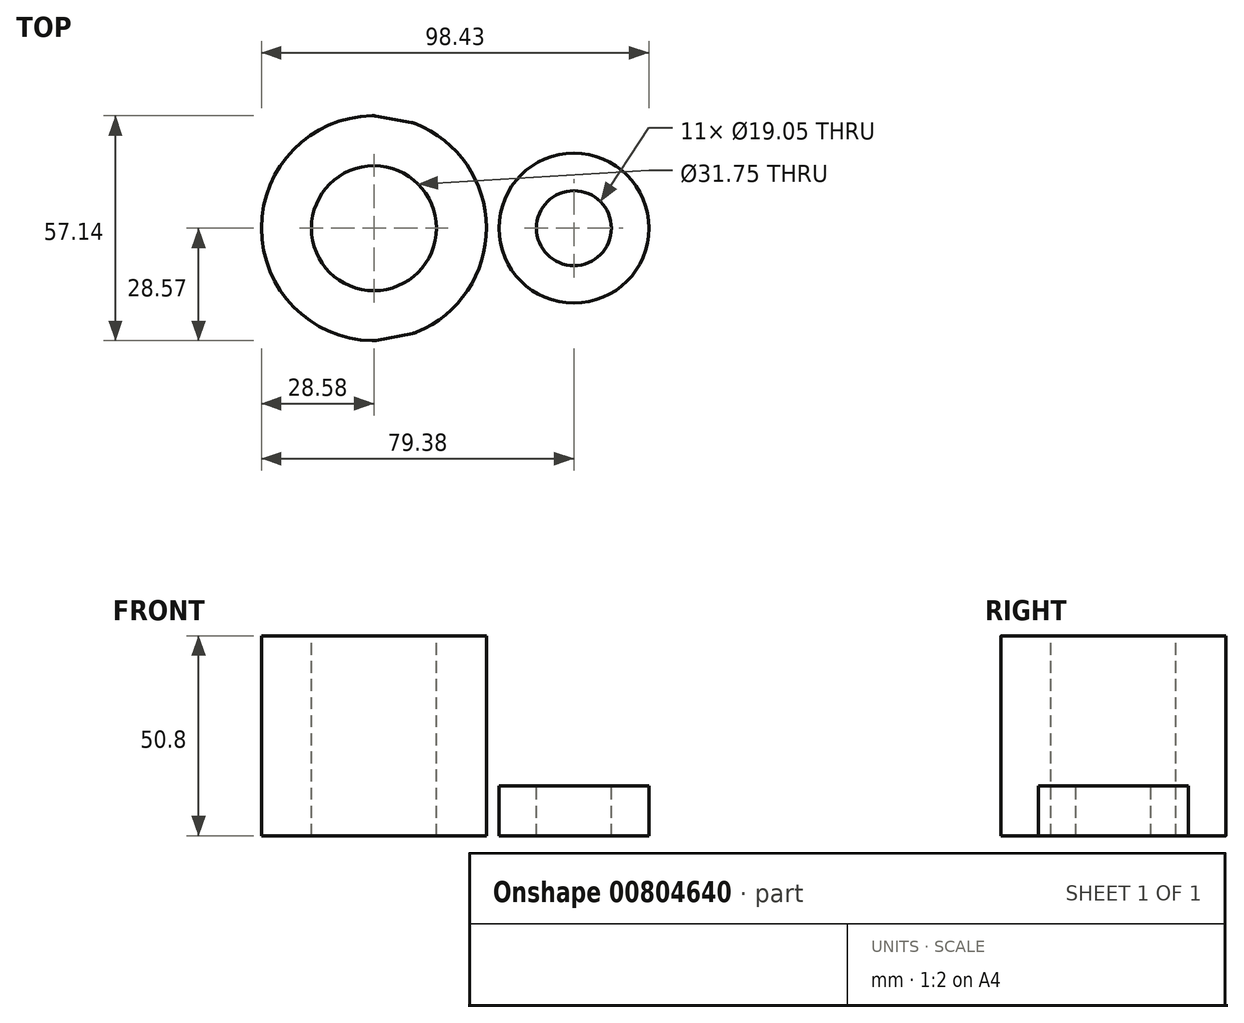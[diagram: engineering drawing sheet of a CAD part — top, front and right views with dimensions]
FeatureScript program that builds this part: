
annotation { "Feature Type Name" : "Feature", "Feature Type Description" : "" }
export const myFeature = defineFeature(function(context is Context, id is Id, definition is map)
    precondition{}
    {
        {
            var Q0;
            Q0=qCreatedBy(makeId("Top.planeOp"),FACE);
            var sketch = newSketch(context, id + "F0", { "sketchPlane" : qUnion([Q0])});
            skCircle(sketch, "E0", {"center": v(0, 0) * mm, "radius": 28.58 * mm});
            skCircle(sketch, "E1", {"center": v(50.8, 0) * mm, "radius": 19.05 * mm});
            skLineSegment(sketch, "E2", {"start": v(0, 28.58) * mm, "end": v(54.2, 18.74) * mm});
            skLineSegment(sketch, "E3", {"start": v(0, -28.57) * mm, "end": v(50.8, -19.05) * mm});
            skCircle(sketch, "E4", {"center": v(0, 0) * mm, "radius": 15.88 * mm});
            skCircle(sketch, "E5", {"center": v(50.8, 0) * mm, "radius": 9.53 * mm});
            skSolve(sketch);
        }
        {
            var Q0;
            Q0=makeQuery(id+"F0.imprint","IMPRINT",FACE,{"disambiguationData":[TD([[makeQuery(id+"F0.imprint","IMPRINT",EDGE,{"derivedFrom":sQuery(id+"F0.wireOp",EDGE,"E4")}),-1.0]])]});
            var Q1;
            {var subQ0=sQuery(id+"F0.wireOp",EDGE,"E2");var subQ1=sQuery(id+"F0.wireOp",EDGE,"E0");var subQ2=makeQuery(id+"F0.imprint","INTERSECT",VERTEX,{"disambiguationData":[OD(1.0)],"derivedFrom":[subQ1,subQ0]});Q1=makeQuery(id+"F0.imprint","IMPRINT",FACE,{"disambiguationData":[TD([[makeQuery(id+"F0.imprint","IMPRINT",EDGE,{"disambiguationData":[TD([[subQ2,1.0]])],"derivedFrom":subQ1}),-1.0]])]});}
            var Q2;
            Q2=makeQuery(id+"F0.imprint","IMPRINT",FACE,{"disambiguationData":[TD([[makeQuery(id+"F0.imprint","IMPRINT",EDGE,{"derivedFrom":sQuery(id+"F0.wireOp",EDGE,"E5")}),-1.0]])]});
            extrude(context, id + "F1", {"entities" : qUnion([Q0, Q1, Q2]), "oppositeDirection" : true, "depth" : 25.4 * mm, "offsetDistance" : 25.4 * mm});
        }
        {
            var Q0;
            Q0=makeQuery(id+"F0.imprint","IMPRINT",FACE,{"disambiguationData":[TD([[makeQuery(id+"F0.imprint","IMPRINT",EDGE,{"derivedFrom":sQuery(id+"F0.wireOp",EDGE,"E4")}),-1.0]])]});
            extrude(context, id + "F2", {"entities" : qUnion([Q0]), "operationType" : NewBodyOperationType.ADD, "depth" : 25.4 * mm, "offsetDistance" : 25.4 * mm});
        }
        {
            var Q0;
            Q0=makeQuery(id+"F0.imprint","IMPRINT",FACE,{"disambiguationData":[TD([[makeQuery(id+"F0.imprint","IMPRINT",EDGE,{"derivedFrom":sQuery(id+"F0.wireOp",EDGE,"E5")}),-1.0]])]});
            extrude(context, id + "F3", {"entities" : qUnion([Q0]), "operationType" : NewBodyOperationType.REMOVE, "oppositeDirection" : true, "depth" : 12.7 * mm, "offsetDistance" : 25.4 * mm});
        }
        {
            var Q0;
            {var subQ0=sQuery(id+"F0.wireOp",EDGE,"E3");var subQ1=sQuery(id+"F0.wireOp",EDGE,"E1");Q0=makeQuery(id+"F3.boolean.opBoolean","SPLIT",EDGE,{"disambiguationData":[topologyDisambiguationEdgeConnected([makeQuery(id+"F3.opExtrude","SWEPT_FACE",FACE,{"disambiguationData":[OSD([subQ1])]})])],"derivedFrom":makeQuery(id+"F1.opExtrude","SWEPT_EDGE",EDGE,{"disambiguationData":[OSD([subQ1,subQ0])]})});}
            var Q1;
            {var subQ0=sQuery(id+"F0.wireOp",EDGE,"E2");var subQ1=sQuery(id+"F0.wireOp",EDGE,"E1");Q1=makeQuery(id+"F3.boolean.opBoolean","SPLIT",EDGE,{"disambiguationData":[topologyDisambiguationEdgeConnected([makeQuery(id+"F3.opExtrude","SWEPT_FACE",FACE,{"disambiguationData":[OSD([subQ1])]})])],"derivedFrom":makeQuery(id+"F1.opExtrude","SWEPT_EDGE",EDGE,{"disambiguationData":[OSD([subQ1,subQ0])]})});}
            fillet(context, id + "F4", {"entities" : qUnion([Q0, Q1]), "radius" : 5.08 * mm, "tangentPropagation" : true, "allowEdgeOverflow" : false});
        }
    });
